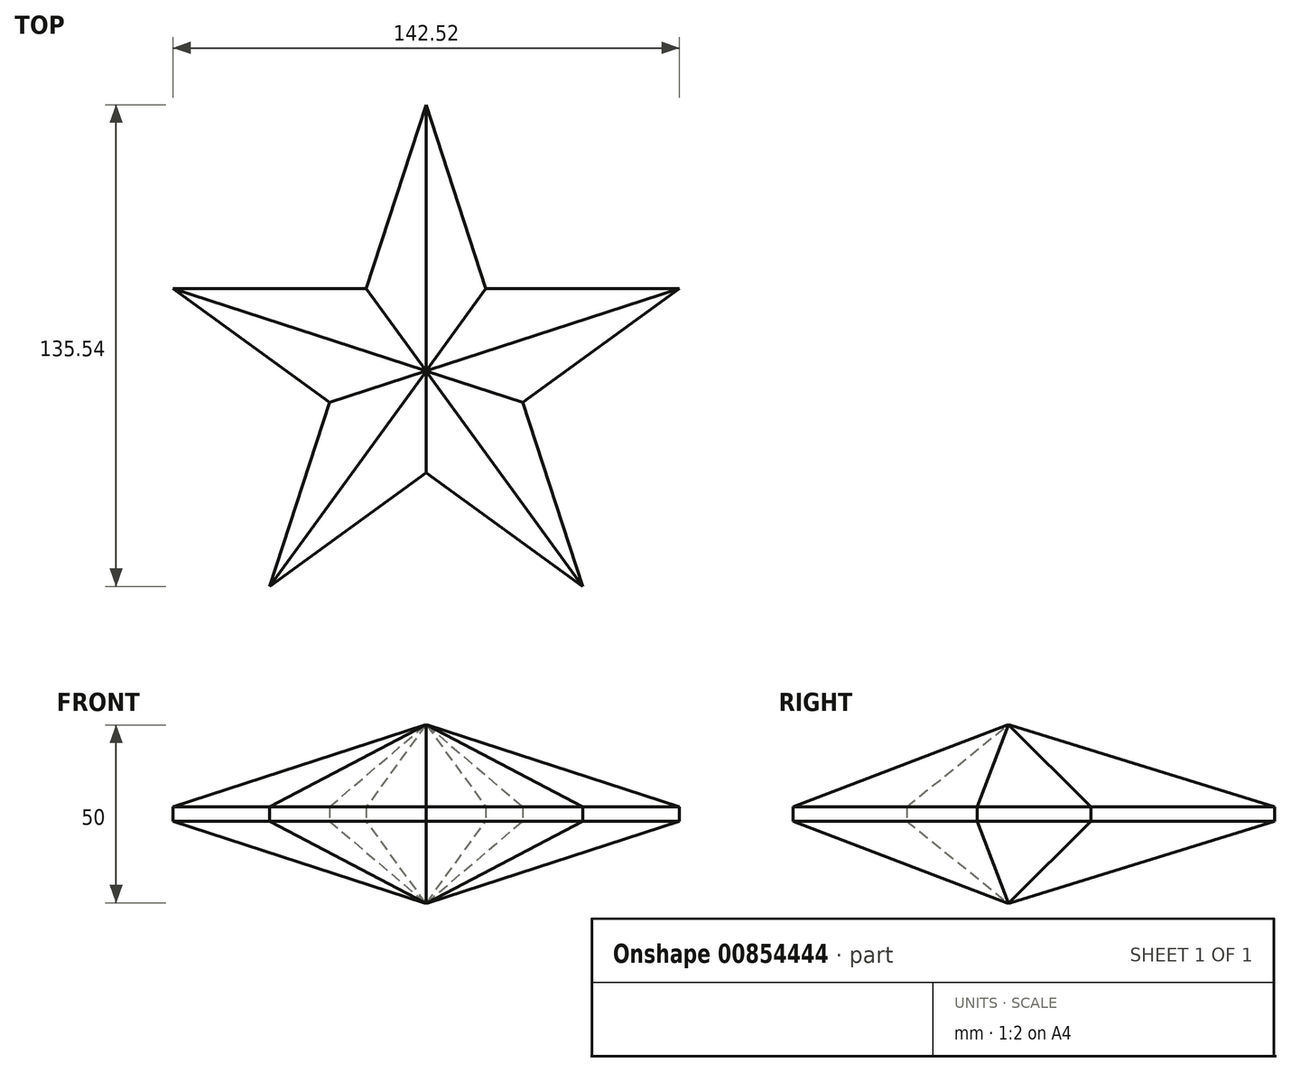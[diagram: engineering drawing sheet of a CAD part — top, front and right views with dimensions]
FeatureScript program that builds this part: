
annotation { "Feature Type Name" : "Feature", "Feature Type Description" : "" }
export const myFeature = defineFeature(function(context is Context, id is Id, definition is map)
    precondition{}
    {
        {
            var Q0;
            Q0=qCreatedBy(makeId("Top.planeOp"),FACE);
            var sketch = newSketch(context, id + "F0", { "sketchPlane" : qUnion([Q0])});
            skCircle(sketch, "E0.cCircle", {"center": v(0, 0) * mm, "radius": 74.92 * mm, "construction": true});
            skLineSegment(sketch, "E0.0", {"start": v(0, 74.92) * mm, "end": v(71.26, 23.15) * mm});
            skLineSegment(sketch, "E0.1", {"start": v(71.26, 23.15) * mm, "end": v(44.04, -60.62) * mm});
            skLineSegment(sketch, "E0.2", {"start": v(44.04, -60.62) * mm, "end": v(-44.04, -60.62) * mm});
            skLineSegment(sketch, "E0.3", {"start": v(-44.04, -60.62) * mm, "end": v(-71.26, 23.15) * mm});
            skLineSegment(sketch, "E0.4", {"start": v(-71.26, 23.15) * mm, "end": v(0, 74.92) * mm});
            skLineSegment(sketch, "E1", {"start": v(0, 74.92) * mm, "end": v(-44.04, -60.62) * mm});
            skLineSegment(sketch, "E2", {"start": v(0, 74.92) * mm, "end": v(44.04, -60.62) * mm});
            skLineSegment(sketch, "E3", {"start": v(-44.04, -60.62) * mm, "end": v(71.26, 23.15) * mm});
            skLineSegment(sketch, "E4", {"start": v(-71.26, 23.15) * mm, "end": v(71.26, 23.15) * mm});
            skLineSegment(sketch, "E5", {"start": v(-71.26, 23.15) * mm, "end": v(44.04, -60.62) * mm});
            skSolve(sketch);
        }
        {
            var Q0;
            {var subQ1=sQuery(id+"F0.wireOp",EDGE,"E1");var subQ3=sQuery(id+"F0.wireOp",EDGE,"E4");var subQ4=makeQuery(id+"F0.imprint","INTERSECT",VERTEX,{"derivedFrom":[subQ1,subQ3]});Q0=makeQuery(id+"F0.imprint","IMPRINT",FACE,{"disambiguationData":[TD([[makeQuery(id+"F0.imprint","IMPRINT",EDGE,{"disambiguationData":[TD([[subQ4,-1.0]])],"derivedFrom":subQ3}),1.0]])]});}
            var Q1;
            {var subQ0=sQuery(id+"F0.wireOp",EDGE,"E4");var subQ1=sQuery(id+"F0.wireOp",EDGE,"E1");var subQ2=makeQuery(id+"F0.imprint","INTERSECT",VERTEX,{"derivedFrom":[subQ1,subQ0]});Q1=makeQuery(id+"F0.imprint","IMPRINT",FACE,{"disambiguationData":[TD([[makeQuery(id+"F0.imprint","IMPRINT",EDGE,{"disambiguationData":[TD([[subQ2,-1.0]])],"derivedFrom":subQ1}),-1.0]])]});}
            var Q2;
            {var subQ0=sQuery(id+"F0.wireOp",EDGE,"E4");var subQ1=sQuery(id+"F0.wireOp",EDGE,"E2");var subQ2=makeQuery(id+"F0.imprint","INTERSECT",VERTEX,{"derivedFrom":[subQ1,subQ0]});Q2=makeQuery(id+"F0.imprint","IMPRINT",FACE,{"disambiguationData":[TD([[makeQuery(id+"F0.imprint","IMPRINT",EDGE,{"disambiguationData":[TD([[subQ2,-1.0]])],"derivedFrom":subQ1}),1.0]])]});}
            var Q3;
            {var subQ1=sQuery(id+"F0.wireOp",EDGE,"E1");var subQ3=sQuery(id+"F0.wireOp",EDGE,"E5");var subQ4=makeQuery(id+"F0.imprint","INTERSECT",VERTEX,{"derivedFrom":[subQ1,subQ3]});Q3=makeQuery(id+"F0.imprint","IMPRINT",FACE,{"disambiguationData":[TD([[makeQuery(id+"F0.imprint","IMPRINT",EDGE,{"disambiguationData":[TD([[subQ4,-1.0]])],"derivedFrom":subQ3}),-1.0]])]});}
            var Q4;
            {var subQ1=sQuery(id+"F0.wireOp",EDGE,"E2");var subQ3=sQuery(id+"F0.wireOp",EDGE,"E3");var subQ4=makeQuery(id+"F0.imprint","INTERSECT",VERTEX,{"derivedFrom":[subQ1,subQ3]});Q4=makeQuery(id+"F0.imprint","IMPRINT",FACE,{"disambiguationData":[TD([[makeQuery(id+"F0.imprint","IMPRINT",EDGE,{"disambiguationData":[TD([[subQ4,1.0]])],"derivedFrom":subQ3}),-1.0]])]});}
            var Q5;
            {var subQ0=sQuery(id+"F0.wireOp",EDGE,"E4");var subQ1=sQuery(id+"F0.wireOp",EDGE,"E1");var subQ2=makeQuery(id+"F0.imprint","INTERSECT",VERTEX,{"derivedFrom":[subQ1,subQ0]});Q5=makeQuery(id+"F0.imprint","IMPRINT",FACE,{"disambiguationData":[TD([[makeQuery(id+"F0.imprint","IMPRINT",EDGE,{"disambiguationData":[TD([[subQ2,-1.0]])],"derivedFrom":subQ1}),1.0]])]});}
            extrude(context, id + "F1", {"entities" : qUnion([Q0, Q1, Q2, Q3, Q4, Q5]), "depth" : 25 * mm, "offsetDistance" : 25 * mm});
        }
        {
            var Q0;
            Q0=makeQuery(id+"F1.opExtrude","CAP_FACE",FACE,{"disambiguationData":[OSD([sQuery(id+"F0.wireOp",EDGE,"E1"),sQuery(id+"F0.wireOp",EDGE,"E2"),sQuery(id+"F0.wireOp",EDGE,"E3"),sQuery(id+"F0.wireOp",EDGE,"E4"),sQuery(id+"F0.wireOp",EDGE,"E5")])],"isStart":false});
            chamfer(context, id + "F2", {"entities" : qUnion([Q0]), "width" : 23 * mm, "tangentPropagation" : true});
        }
        {
            var Q0;
            Q0=makeQuery(id+"F1.opExtrude","SWEPT_BODY",BODY,{"disambiguationData":[OSD([sQuery(id+"F0.wireOp",EDGE,"E1"),sQuery(id+"F0.wireOp",EDGE,"E2"),sQuery(id+"F0.wireOp",EDGE,"E3"),sQuery(id+"F0.wireOp",EDGE,"E4"),sQuery(id+"F0.wireOp",EDGE,"E5")])]});
            var Q1;
            Q1=qCreatedBy(makeId("Top.planeOp"),FACE);
            mirror(context, id + "F3", {"operationType" : NewBodyOperationType.ADD, "entities" : qUnion([Q0]), "mirrorPlane" : qUnion([Q1])});
        }
    });
